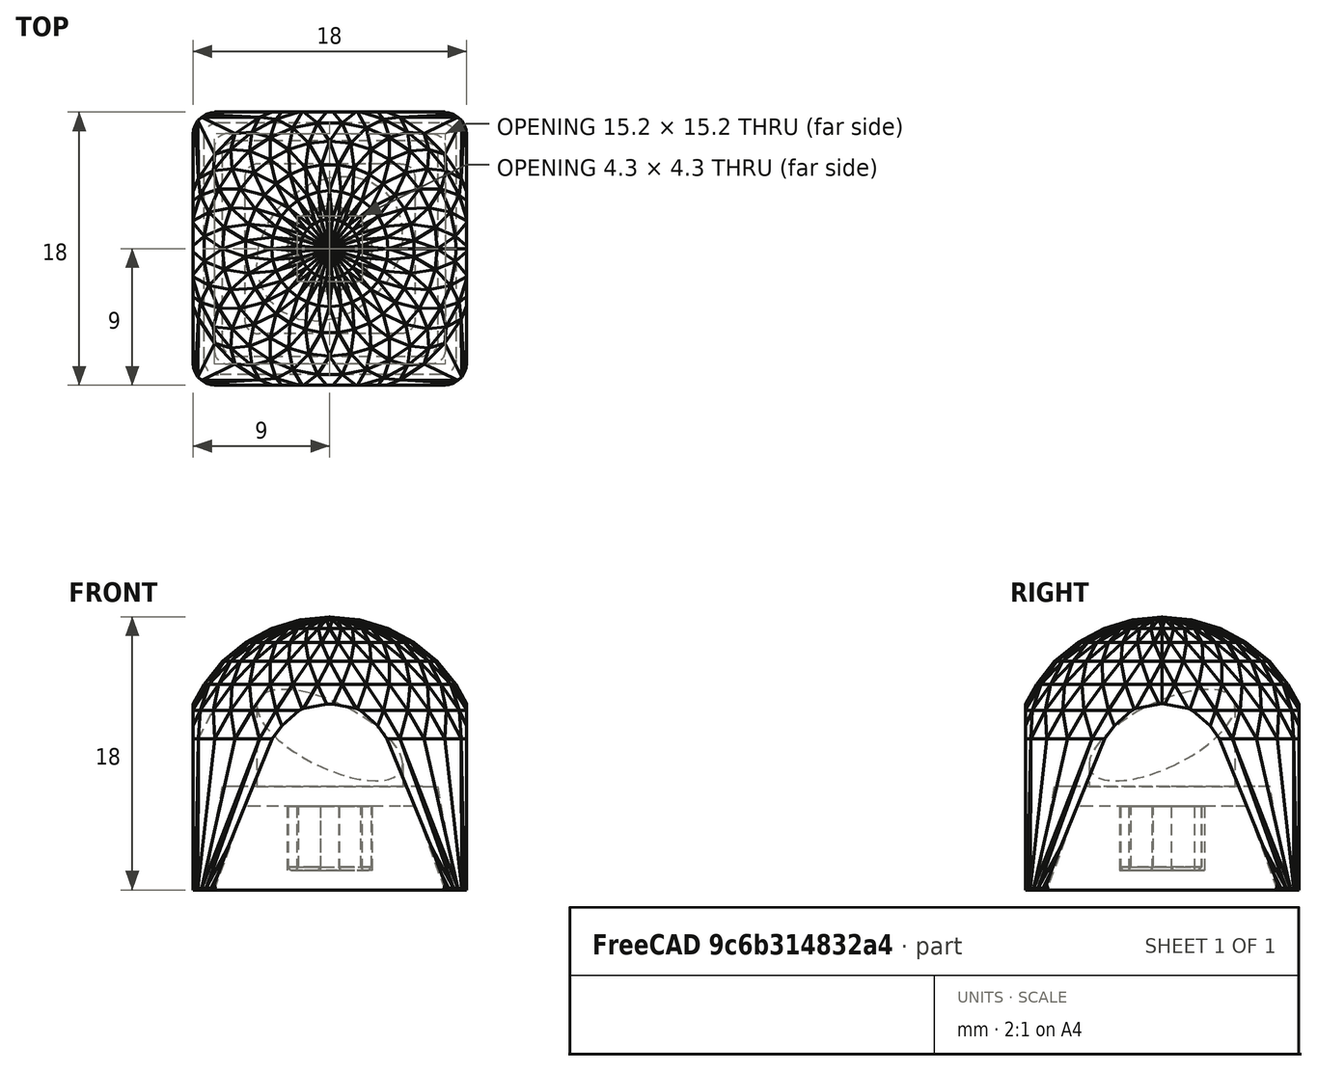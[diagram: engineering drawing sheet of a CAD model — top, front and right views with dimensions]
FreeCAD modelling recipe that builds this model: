
FCSTD DOCUMENT  (FreeCAD 1.0R39319 (Git))
Label: dome-profile-1u
License: All rights reserved
LicenseURL: https://en.wikipedia.org/wiki/All_rights_reserved
objects: Part::Box×12, Part::Cut×12, Part::Fillet×8, Part::MultiFuse×7, Part::Feature×6, Part::Cylinder×4, Part::MultiCommon×1, Part::Chamfer×1, Part::Part2DObjectPython×1, Part::Extrusion×1
note: 53 computed .brp shape members not serialized (recipe doc carries the construction recipe); baked Part::Feature solids carry a one-line shape summary decoded from their .brp

FEATURE [Part::Cylinder] Cylinder  label="円柱"
  Angle = 360
  AttacherType = Attacher::AttachEngine3D
  FirstAngle = 0
  Height = 4.2
  Placement = pos=(0,0,1.3) rot=(0,0,1;0rad)
  Radius = 2.75
  SecondAngle = 0
FEATURE [Part::Box] Box  label="立方体"
  AttacherType = Attacher::AttachEngine3D
  Height = 4.2
  Length = 4.1
  Placement = pos=(-2.05,-0.585,1.3) rot=(0,0,1;0rad)
  Width = 1.17
FEATURE [Part::Box] Box001  label="立方体001"
  AttacherType = Attacher::AttachEngine3D
  Height = 4.2
  Length = 1.17
  Placement = pos=(-0.58,-2.05,1.3) rot=(0,0,1;0rad)
  Width = 5.1
FEATURE [Part::MultiFuse] Fusion
  Shapes = -> [Box,Box001]
FEATURE [Part::Cut] Cut
  Base = -> Cylinder
  Tool = -> Fusion
FEATURE [Part::Box] Box006  label="立方体006"
  AttacherType = Attacher::AttachEngine3D
  Height = 18.1
  Length = 18
  Placement = pos=(-9,-9,0) rot=(0,0,1;0rad)
  Width = 18
FEATURE [Part::Fillet] Fillet004
  Base = -> Box006
  EdgeLinks = -> Box006 [Edge1,Edge3,Edge5,Edge7]
  Edges = 4 edges r=1.5: [Edge1,Edge3,Edge5,Edge7]
FEATURE [Part::Feature] hull
  shape: bbox 20 x 20 x 20 mm, 642 faces (baked)
FEATURE [Part::MultiCommon] Common
  Shapes = -> [hull,Fillet004]
FEATURE [Part::Fillet] Fillet
  Base = -> Cut
  EdgeLinks = -> Cut [Edge2,Edge18,Edge30,Edge31,Edge34,Edge37]
  Edges = 6 edges r=0.3: [Edge2,Edge18,Edge30,Edge31,Edge34,Edge37]
FEATURE [Part::Chamfer] Chamfer  label="shaft"
  Base = -> Fillet
  EdgeLinks = -> Fillet [Edge7,Edge8,Edge9,Edge10,Edge11,Edge12,Edge13,Edge14,Edge15,Edge16,Edge17,Edge18,Edge19,Edge20,Edge21]
  Edges = 15 edges r=0.2: [Edge7,Edge8,Edge9,Edge10,Edge11,Edge12,Edge13,Edge14,Edge15,Edge16,Edge17,Edge18,Edge19,Edge20,Edge21]
FEATURE [Part::Feature] hull001
  shape: bbox 15.2 x 15.2 x 6.5 mm, 10 faces (baked)
FEATURE [Part::Box] Box010  label="立方体010"
  AttacherType = Attacher::AttachEngine3D
  Height = 1
  Length = 15.2
  Placement = pos=(-7.6,-7.6,-1) rot=(0,0,1;0rad)
  Width = 15.2
FEATURE [Part::Cut] Cut002
  Base = -> hull001
  Tool = -> Box010
FEATURE [Part::Fillet] Fillet006
  Base = -> Cut002
  EdgeLinks = -> Cut002 [Edge1,Edge3,Edge6,Edge10]
  Edges = 4 edges r=1: [Edge1,Edge3,Edge6,Edge10]
FEATURE [Part::Box] Box012  label="立方体012"
  AttacherType = Attacher::AttachEngine3D
  Height = 1
  Length = 15.2
  Placement = pos=(-7.6,-7.6,-1) rot=(0,0,1;0rad)
  Width = 15.2
FEATURE [Part::Box] Box013  label="立方体013"
  AttacherType = Attacher::AttachEngine3D
  Height = 1
  Length = 16.6
  Placement = pos=(-8.3,-8.3,-1) rot=(0,0,1;0rad)
  Width = 16.6
FEATURE [Part::Feature] hull003
  shape: bbox 15.2 x 15.2 x 6.5 mm, 10 faces (baked)
FEATURE [Part::Cut] Cut004
  Base = -> hull003
  Tool = -> Box012
FEATURE [Part::Fillet] Fillet008
  Base = -> Cut004
  EdgeLinks = -> Cut004 [Edge1,Edge3,Edge6,Edge10]
  Edges = 4 edges r=1: [Edge1,Edge3,Edge6,Edge10]
FEATURE [Part::Feature] hull004
  shape: bbox 16.6 x 16.6 x 7.8 mm, 10 faces (baked)
FEATURE [Part::Cut] Cut005
  Base = -> hull004
  Tool = -> Box013
FEATURE [Part::Fillet] Fillet009
  Base = -> Cut005
  EdgeLinks = -> Cut005 [Edge1,Edge3,Edge6,Edge10]
  Edges = 4 edges r=1: [Edge1,Edge3,Edge6,Edge10]
FEATURE [Part::Cut] Cut006
  Base = -> Fillet009
  Tool = -> Fillet008
FEATURE [Part::Box] Box014  label="立方体014"
  AttacherType = Attacher::AttachEngine3D
  Height = 4.2
  Length = 4.3
  Placement = pos=(-2.15,-0.63,1.3) rot=(0,0,1;0rad)
  Width = 1.27
FEATURE [Part::Box] Box015  label="立方体015"
  AttacherType = Attacher::AttachEngine3D
  Height = 4.2
  Length = 1.27
  Placement = pos=(-0.63,-2.15,1.3) rot=(0,0,1;0rad)
  Width = 4.3
FEATURE [Part::Cylinder] Cylinder001  label="円柱001"
  Angle = 360
  AttacherType = Attacher::AttachEngine3D
  FirstAngle = 0
  Height = 4.2
  Placement = pos=(0,0,1.3) rot=(0,0,1;0rad)
  Radius = 2.8
  SecondAngle = 0
FEATURE [Part::MultiFuse] Fusion002
  Shapes = -> [Box014,Box015]
FEATURE [Part::Cut] Cut007
  Base = -> Cylinder001
  Tool = -> Fusion002
FEATURE [Part::Cut] Cut008
  Base = -> Common
  Tool = -> Fillet006
FEATURE [Part::MultiFuse] Fusion004
  Shapes = -> [Cut008,Chamfer]
FEATURE [Part::Fillet] Fillet012  label="dome_profile"
  Base = -> Fusion004
  EdgeLinks = -> Fusion004 [Edge696]
  Edges = 1 edges r=0.5: [Edge696]
FEATURE [Part::MultiFuse] Fusion005  label="encapsuled_base"
  Shapes = -> [Cut007,Cut006]
FEATURE [Part::Part2DObjectPython] Circle  # Draft 2D object (typed FeaturePython)
  Area = 86.5901
  FirstAngle = 0
  LastAngle = 0
  MakeFace = true
  Placement = pos=(0,0,10.2) rot=(1,1,0;0.610865rad)
  Radius = 5.25
FEATURE [Part::Box] Box016  label="立方体016"
  AttacherType = Attacher::AttachEngine3D
  Height = 1
  Length = 15.2
  Placement = pos=(-7.6,-7.6,-1) rot=(0,0,1;0rad)
  Width = 15.2
FEATURE [Part::Box] Box017  label="立方体017"
  AttacherType = Attacher::AttachEngine3D
  Height = 1
  Length = 16.6
  Placement = pos=(-8.3,-8.3,-1) rot=(0,0,1;0rad)
  Width = 16.6
FEATURE [Part::Box] Box018  label="立方体018"
  AttacherType = Attacher::AttachEngine3D
  Height = 4.2
  Length = 4.3
  Placement = pos=(-2.15,-0.63,1.3) rot=(0,0,1;0rad)
  Width = 1.27
FEATURE [Part::Box] Box019  label="立方体019"
  AttacherType = Attacher::AttachEngine3D
  Height = 4.2
  Length = 1.27
  Placement = pos=(-0.63,-2.15,1.3) rot=(0,0,1;0rad)
  Width = 4.3
FEATURE [Part::Cylinder] Cylinder002  label="円柱002"
  Angle = 360
  AttacherType = Attacher::AttachEngine3D
  FirstAngle = 0
  Height = 4.2
  Placement = pos=(0,0,1.3) rot=(0,0,1;0rad)
  Radius = 2.8
  SecondAngle = 0
FEATURE [Part::MultiFuse] Fusion006
  Shapes = -> [Box018,Box019]
FEATURE [Part::Cut] Cut012
  Base = -> Cylinder002
  Tool = -> Fusion006
FEATURE [Part::Feature] hull005
  shape: bbox 15.2 x 15.2 x 6.5 mm, 10 faces (baked)
FEATURE [Part::Cut] Cut009
  Base = -> hull005
  Tool = -> Box016
FEATURE [Part::Fillet] Fillet013
  Base = -> Cut009
  EdgeLinks = -> Cut009 [Edge1,Edge3,Edge6,Edge10]
  Edges = 4 edges r=1: [Edge1,Edge3,Edge6,Edge10]
FEATURE [Part::Feature] hull006
  shape: bbox 16.6 x 16.6 x 7.8 mm, 10 faces (baked)
FEATURE [Part::Cut] Cut010
  Base = -> hull006
  Tool = -> Box017
FEATURE [Part::Fillet] Fillet014
  Base = -> Cut010
  EdgeLinks = -> Cut010 [Edge1,Edge3,Edge6,Edge10]
  Edges = 4 edges r=1: [Edge1,Edge3,Edge6,Edge10]
FEATURE [Part::Cut] Cut011
  Base = -> Fillet014
  Tool = -> Fillet013
FEATURE [Part::MultiFuse] Fusion007
  Shapes = -> [Cut012,Cut011]
FEATURE [Part::Extrusion] Extrude
  Base = -> Circle
  Dir = (0,0,-1)
  DirMode = 0
  FaceMakerClass = Part::FaceMakerBullseye
  FaceMakerMode = 3
  LengthFwd = 7
  LengthRev = 0
  Solid = false
  Symmetric = false
FEATURE [Part::Cylinder] Cylinder003  label="円柱003"
  Angle = 360
  AttacherType = Attacher::AttachEngine3D
  FirstAngle = 0
  Height = 6.8
  Radius = 6
  SecondAngle = 0
FEATURE [Part::Cut] Cut013
  Base = -> Extrude
  Tool = -> Cylinder003
FEATURE [Part::MultiFuse] Fusion008  label="logo_base"
  Shapes = -> [Fusion007,Cut013]
